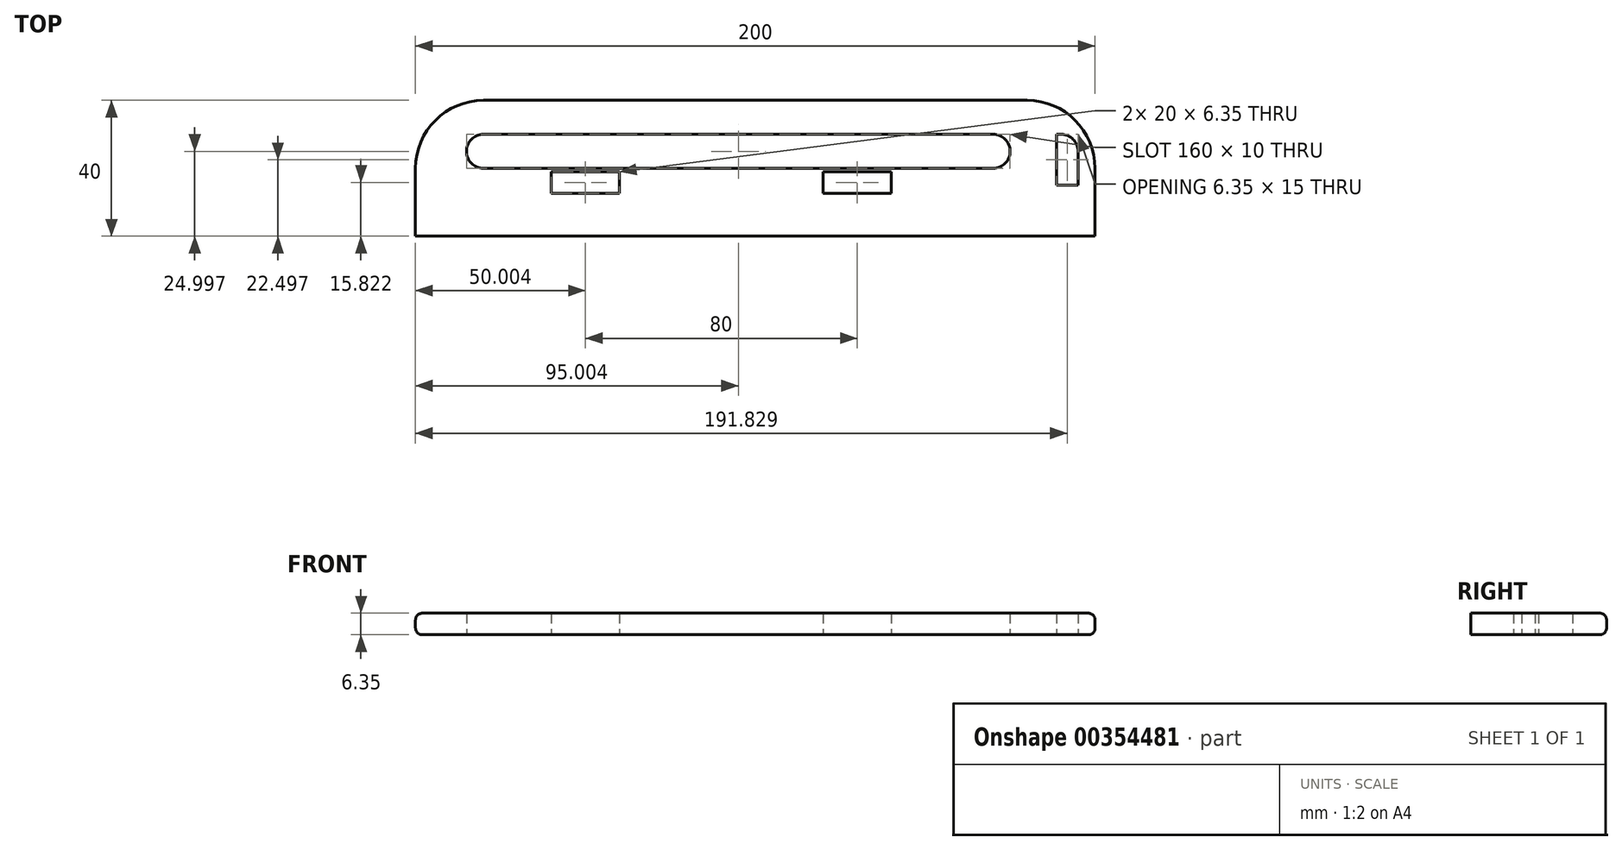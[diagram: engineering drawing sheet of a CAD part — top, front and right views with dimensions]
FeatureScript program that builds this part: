
annotation { "Feature Type Name" : "Feature", "Feature Type Description" : "" }
export const myFeature = defineFeature(function(context is Context, id is Id, definition is map)
    precondition{}
    {
        {
            var Q0;
            Q0=qCreatedBy(makeId("Top.planeOp"),FACE);
            var sketch = newSketch(context, id + "F0", { "sketchPlane" : qUnion([Q0])});
            skLineSegment(sketch, "E0.bottom", {"start": v(-77.86, 9.4) * mm, "end": v(82.14, 9.4) * mm});
            skLineSegment(sketch, "E0.top", {"start": v(-97.86, -30.6) * mm, "end": v(102.14, -30.6) * mm});
            skLineSegment(sketch, "E0.left", {"start": v(-97.86, -10.6) * mm, "end": v(-97.86, -30.6) * mm});
            skLineSegment(sketch, "E0.right", {"start": v(102.14, -10.6) * mm, "end": v(102.14, -30.6) * mm});
            skPoint(sketch, "E1.visualSharp", {"position": v(-97.86, 9.4) * mm});
            skArc(sketch, "E1.filletArc", {"start": v(-77.86, 9.4) * mm, "mid": v(-92, 3.55) * mm, "end": v(-97.86, -10.6) * mm});
            skPoint(sketch, "E2.visualSharp", {"position": v(102.14, 9.4) * mm});
            skArc(sketch, "E2.filletArc", {"start": v(102.14, -10.6) * mm, "mid": v(96.29, 3.55) * mm, "end": v(82.14, 9.4) * mm});
            skLineSegment(sketch, "E3.bottom", {"start": v(-77.86, -0.6) * mm, "end": v(72.14, -0.6) * mm});
            skLineSegment(sketch, "E3.top", {"start": v(-77.86, -10.6) * mm, "end": v(72.14, -10.6) * mm});
            skLineSegment(sketch, "E3.left", {"start": v(-77.86, -0.6) * mm, "end": v(-77.86, -10.6) * mm});
            skLineSegment(sketch, "E3.right", {"start": v(72.14, -0.6) * mm, "end": v(72.14, -10.6) * mm});
            skCircle(sketch, "E4", {"center": v(72.14, -5.6) * mm, "radius": 5 * mm});
            skCircle(sketch, "E5", {"center": v(-77.86, -5.6) * mm, "radius": 5 * mm});
            skLineSegment(sketch, "E6.bottom", {"start": v(-57.86, -11.6) * mm, "end": v(-37.86, -11.6) * mm});
            skLineSegment(sketch, "E6.top", {"start": v(-57.86, -17.94) * mm, "end": v(-37.86, -17.94) * mm});
            skLineSegment(sketch, "E6.left", {"start": v(-57.86, -11.6) * mm, "end": v(-57.86, -17.94) * mm});
            skLineSegment(sketch, "E6.right", {"start": v(-37.86, -11.6) * mm, "end": v(-37.86, -17.94) * mm});
            skLineSegment(sketch, "E7.bottom", {"start": v(22.14, -11.6) * mm, "end": v(42.14, -11.6) * mm});
            skLineSegment(sketch, "E7.top", {"start": v(22.14, -17.94) * mm, "end": v(42.14, -17.94) * mm});
            skLineSegment(sketch, "E7.left", {"start": v(22.14, -11.6) * mm, "end": v(22.14, -17.94) * mm});
            skLineSegment(sketch, "E7.right", {"start": v(42.14, -11.6) * mm, "end": v(42.14, -17.94) * mm});
            skLineSegment(sketch, "E8.bottom", {"start": v(90.8, -0.6) * mm, "end": v(92.14, -0.6) * mm});
            skLineSegment(sketch, "E8.top", {"start": v(90.8, -15.6) * mm, "end": v(97.14, -15.6) * mm});
            skLineSegment(sketch, "E8.left", {"start": v(90.8, -0.6) * mm, "end": v(90.8, -15.6) * mm});
            skLineSegment(sketch, "E8.right", {"start": v(97.14, -5.6) * mm, "end": v(97.14, -15.6) * mm});
            skLineSegment(sketch, "E9.bottom", {"start": v(-67.86, -30.6) * mm, "end": v(-47.86, -30.6) * mm});
            skLineSegment(sketch, "E9.top", {"start": v(-67.86, -36.94) * mm, "end": v(-47.86, -36.94) * mm});
            skLineSegment(sketch, "E9.left", {"start": v(-67.86, -30.6) * mm, "end": v(-67.86, -36.94) * mm});
            skLineSegment(sketch, "E9.right", {"start": v(-47.86, -30.6) * mm, "end": v(-47.86, -36.94) * mm});
            skLineSegment(sketch, "E10.bottom", {"start": v(52.14, -30.6) * mm, "end": v(72.14, -30.6) * mm});
            skLineSegment(sketch, "E10.top", {"start": v(52.14, -36.94) * mm, "end": v(72.14, -36.94) * mm});
            skLineSegment(sketch, "E10.left", {"start": v(52.14, -30.6) * mm, "end": v(52.14, -36.94) * mm});
            skLineSegment(sketch, "E10.right", {"start": v(72.14, -30.6) * mm, "end": v(72.14, -36.94) * mm});
            skPoint(sketch, "E11.visualSharp", {"position": v(97.14, -0.6) * mm});
            skArc(sketch, "E11.filletArc", {"start": v(97.14, -5.6) * mm, "mid": v(95.68, -2.06) * mm, "end": v(92.14, -0.6) * mm});
            skSolve(sketch);
        }
        {
            var Q0;
            Q0=makeQuery(id+"F0.imprint","IMPRINT",FACE,{"disambiguationData":[TD([[makeQuery(id+"F0.imprint","IMPRINT",EDGE,{"derivedFrom":sQuery(id+"F0.wireOp",EDGE,"E0.bottom")}),-1.0]])]});
            var Q1;
            Q1=makeQuery(id+"F0.imprint","IMPRINT",FACE,{"disambiguationData":[TD([[makeQuery(id+"F0.imprint","IMPRINT",EDGE,{"derivedFrom":sQuery(id+"F0.wireOp",EDGE,"E9.bottom")}),-1.0]])]});
            var Q2;
            Q2=makeQuery(id+"F0.imprint","IMPRINT",FACE,{"disambiguationData":[TD([[makeQuery(id+"F0.imprint","IMPRINT",EDGE,{"derivedFrom":sQuery(id+"F0.wireOp",EDGE,"E10.bottom")}),-1.0]])]});
            extrude(context, id + "F1", {"entities" : qUnion([Q0, Q1, Q2]), "depth" : 6.35 * mm});
        }
        {
            var Q0;
            Q0=makeQuery(id+"F1.opExtrude","CAP_EDGE",EDGE,{"disambiguationData":[OSD([sQuery(id+"F0.wireOp",EDGE,"E9.top")])],"isStart":false});
            var Q1;
            Q1=makeQuery(id+"F1.opExtrude","CAP_EDGE",EDGE,{"disambiguationData":[OSD([sQuery(id+"F0.wireOp",EDGE,"E10.top")])],"isStart":false});
            var Q2;
            Q2=makeQuery(id+"F1.opExtrude","CAP_EDGE",EDGE,{"disambiguationData":[OSD([sQuery(id+"F0.wireOp",EDGE,"E1.filletArc")])],"isStart":false});
            var Q3;
            Q3=makeQuery(id+"F1.opExtrude","CAP_EDGE",EDGE,{"disambiguationData":[OSD([sQuery(id+"F0.wireOp",EDGE,"E0.bottom")])],"isStart":true});
            fillet(context, id + "F2", {"entities" : qUnion([Q0, Q1, Q2, Q3]), "radius" : 2 * mm, "tangentPropagation" : true, "allowEdgeOverflow" : false});
        }
    });
